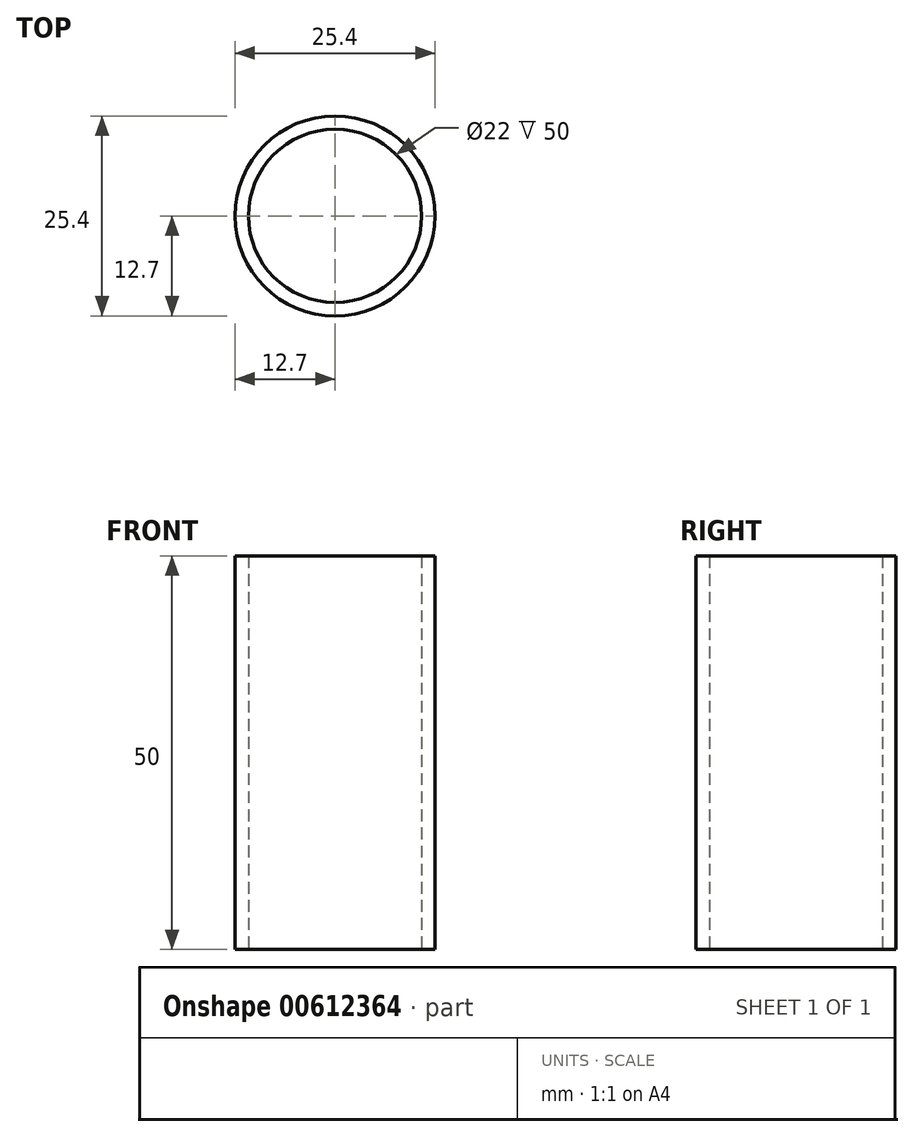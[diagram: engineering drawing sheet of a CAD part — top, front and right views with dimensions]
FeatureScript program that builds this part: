
annotation { "Feature Type Name" : "Feature", "Feature Type Description" : "" }
export const myFeature = defineFeature(function(context is Context, id is Id, definition is map)
    precondition{}
    {
        {
            var Q0;
            Q0=qCreatedBy(makeId("Top.planeOp"),FACE);
            var sketch = newSketch(context, id + "F0", { "sketchPlane" : qUnion([Q0])});
            skCircle(sketch, "E0", {"center": v(0, 0) * mm, "radius": 12.7 * mm});
            skCircle(sketch, "E1", {"center": v(0, 0) * mm, "radius": 11 * mm});
            skSolve(sketch);
        }
        {
            var Q0;
            Q0=makeQuery(id+"F0.imprint","IMPRINT",FACE,{"disambiguationData":[TD([[makeQuery(id+"F0.imprint","IMPRINT",EDGE,{"derivedFrom":sQuery(id+"F0.wireOp",EDGE,"E0")}),1.0]])]});
            extrude(context, id + "F1", {"entities" : qUnion([Q0]), "depth" : 50 * mm, "offsetDistance" : 25 * mm});
        }
    });
